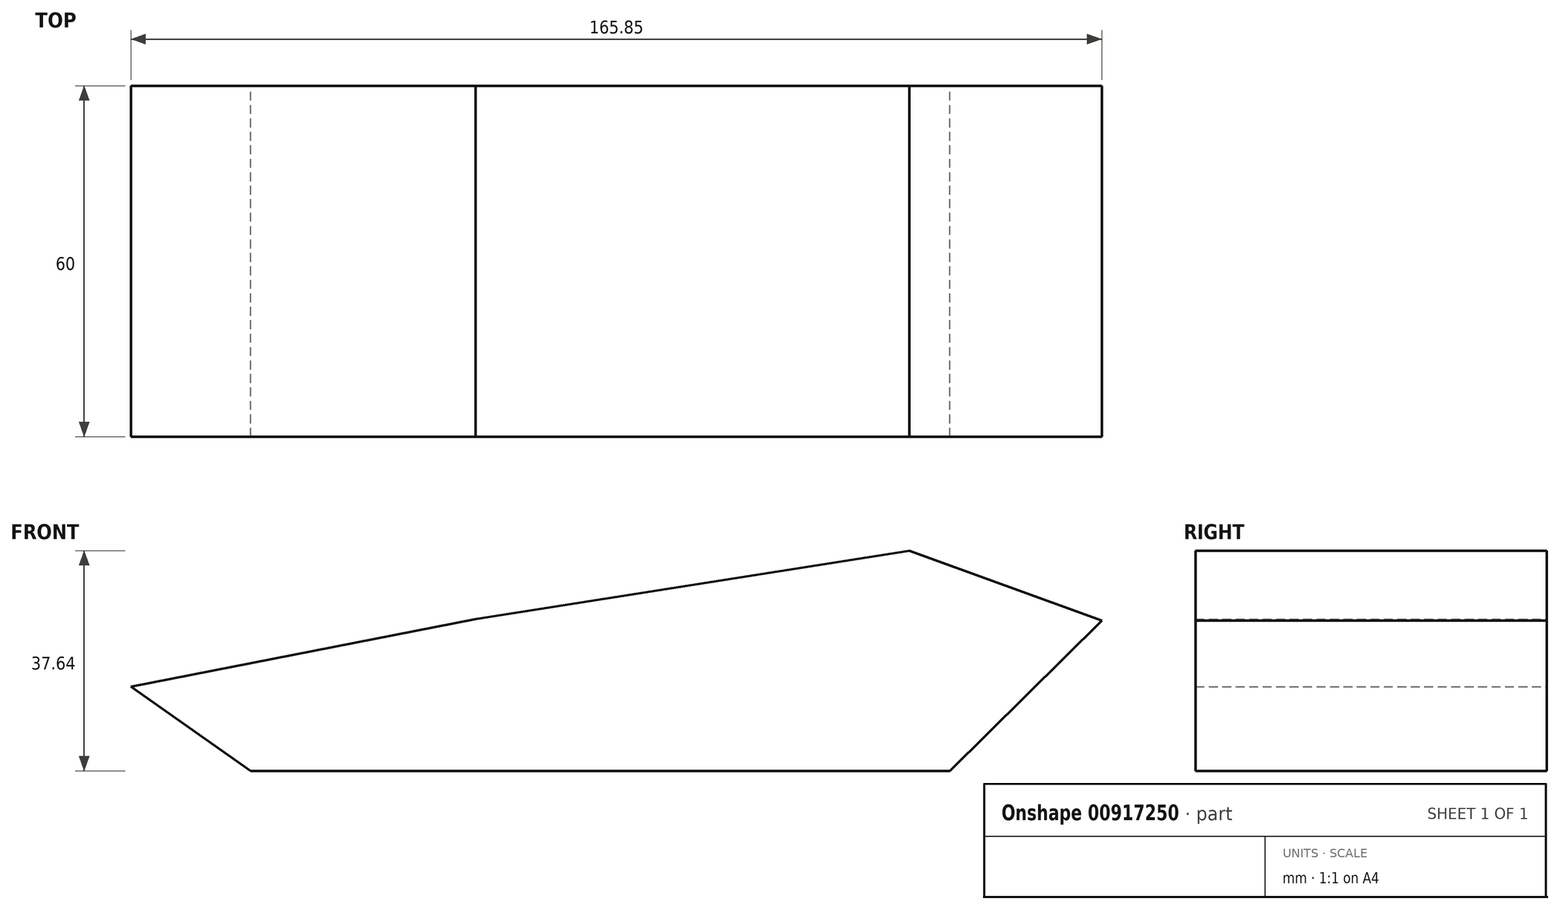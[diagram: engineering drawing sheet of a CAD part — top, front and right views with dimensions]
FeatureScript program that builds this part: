
annotation { "Feature Type Name" : "Feature", "Feature Type Description" : "" }
export const myFeature = defineFeature(function(context is Context, id is Id, definition is map)
    precondition{}
    {
        {
            var Q0;
            Q0=qCreatedBy(makeId("Front.planeOp"),FACE);
            var sketch = newSketch(context, id + "F0", { "sketchPlane" : qUnion([Q0])});
            skLineSegment(sketch, "E0", {"start": v(0, 0) * mm, "end": v(-50, 0) * mm});
            skLineSegment(sketch, "E1", {"start": v(-50, 0) * mm, "end": v(-70.43, 14.4) * mm});
            skPoint(sketch, "E2.orphan", {"position": v(-90.86, 28.82) * mm});
            skLineSegment(sketch, "E3", {"start": v(-70.43, 14.4) * mm, "end": v(-11.55, 25.96) * mm});
            skPoint(sketch, "E4.end.orphan", {"position": v(0, 8.55) * mm});
            skLineSegment(sketch, "E5", {"start": v(-11.55, 25.96) * mm, "end": v(62.53, 37.64) * mm});
            skLineSegment(sketch, "E6", {"start": v(62.53, 37.64) * mm, "end": v(95.42, 25.67) * mm});
            skLineSegment(sketch, "E7", {"start": v(-1.76, 0) * mm, "end": v(69.44, 0) * mm});
            skLineSegment(sketch, "E8", {"start": v(95.42, 25.67) * mm, "end": v(69.44, 0) * mm});
            skLineSegment(sketch, "E9", {"start": v(-11.55, 25.96) * mm, "end": v(94.61, 25.96) * mm});
            skSolve(sketch);
        }
        {
            var Q0;
            Q0 = qSketchRegion(id + "F0", true);
            extrude(context, id + "F1", {"entities" : qUnion([Q0]), "flatOperationType" : FlatOperationType.REMOVE, "depth" : 60 * mm, "offsetDistance" : 25 * mm, "domain" : OperationDomain.MODEL});
        }
    });
